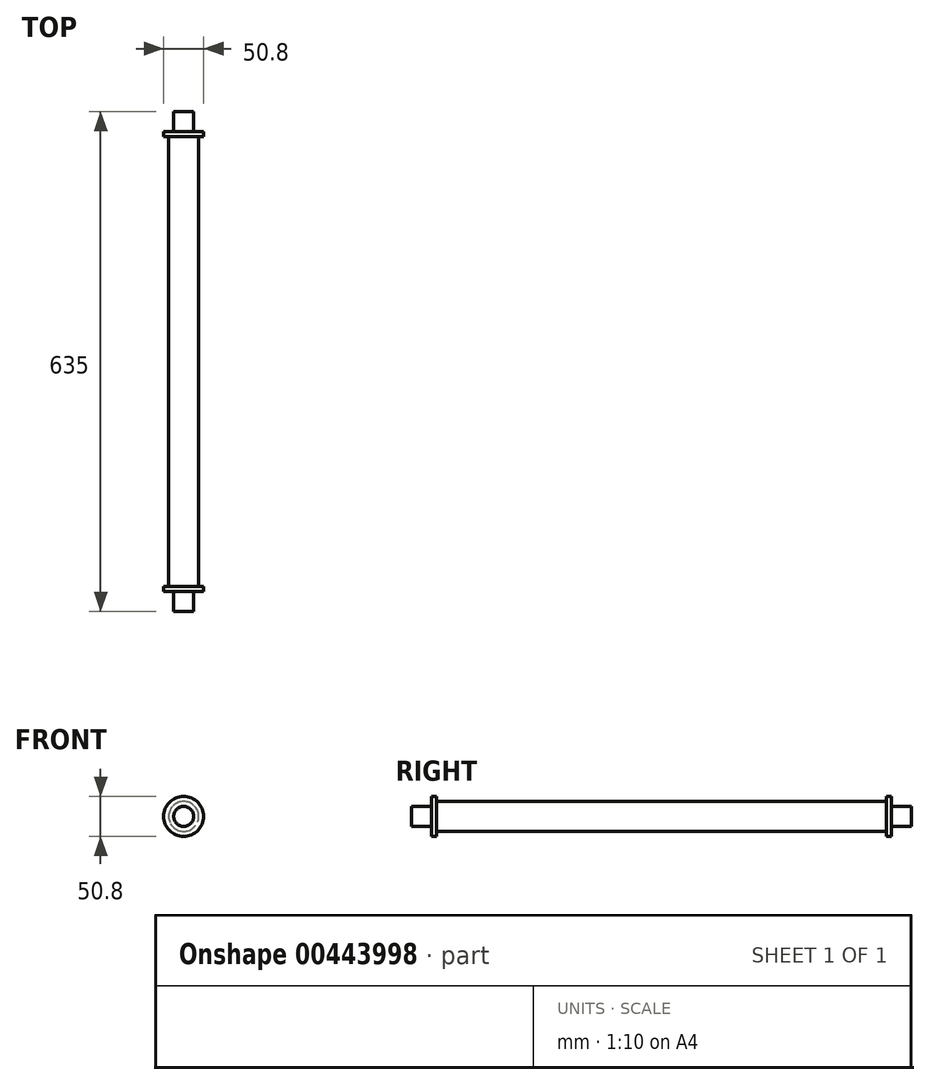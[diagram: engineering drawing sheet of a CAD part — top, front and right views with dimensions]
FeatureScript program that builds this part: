
annotation { "Feature Type Name" : "Feature", "Feature Type Description" : "" }
export const myFeature = defineFeature(function(context is Context, id is Id, definition is map)
    precondition{}
    {
        {
            var Q0;
            Q0=qCreatedBy(makeId("Front.planeOp"),FACE);
            var sketch = newSketch(context, id + "F0", { "sketchPlane" : qUnion([Q0])});
            skCircle(sketch, "E0", {"center": v(0, 0) * mm, "radius": 19.05 * mm});
            skSolve(sketch);
        }
        {
            var Q0;
            Q0 = qSketchRegion(id + "F0", true);
            extrude(context, id + "F1", {"entities" : qUnion([Q0]), "depth" : 584.2 * mm});
        }
        {
            var Q0;
            Q0=makeQuery(id+"F1.opExtrude","CAP_FACE",FACE,{"disambiguationData":[OSD([sQuery(id+"F0.wireOp",EDGE,"E0")])],"isStart":false});
            var sketch = newSketch(context, id + "F2", { "sketchPlane" : qUnion([Q0])});
            skCircle(sketch, "E1", {"center": v(0, 0) * mm, "radius": 25.4 * mm});
            skSolve(sketch);
        }
        {
            var Q0;
            Q0=makeQuery(id+"F1.opExtrude","CAP_FACE",FACE,{"disambiguationData":[OSD([sQuery(id+"F0.wireOp",EDGE,"E0")])],"isStart":true});
            var sketch = newSketch(context, id + "F3", { "sketchPlane" : qUnion([Q0])});
            skCircle(sketch, "E2", {"center": v(0, 0) * mm, "radius": 25.4 * mm});
            skSolve(sketch);
        }
        {
            var Q0;
            Q0 = qSketchRegion(id + "F3", true);
            extrude(context, id + "F4", {"entities" : qUnion([Q0]), "operationType" : NewBodyOperationType.ADD, "oppositeDirection" : true, "depth" : 6.35 * mm});
        }
        {
            var Q0;
            Q0=makeQuery(id+"F2.imprint","IMPRINT",FACE,{"disambiguationData":[TD([[makeQuery(id+"F2.imprint","IMPRINT",EDGE,{"derivedFrom":sQuery(id+"F2.wireOp",EDGE,"E1")}),1.0]])]});
            extrude(context, id + "F5", {"entities" : qUnion([Q0]), "operationType" : NewBodyOperationType.ADD, "oppositeDirection" : true, "depth" : 6.35 * mm});
        }
        {
            var Q0;
            {var subQ0=sQuery(id+"F0.wireOp",EDGE,"E0");Q0=makeQuery(id+"F5.boolean.opBoolean","MERGE",FACE,{"derivedFrom":[makeQuery(id+"F1.opExtrude","CAP_FACE",FACE,{"disambiguationData":[OSD([subQ0])],"isStart":false}),makeQuery(id+"F5.opExtrude","CAP_FACE",FACE,{"disambiguationData":[OSD([subQ0,sQuery(id+"F2.wireOp",EDGE,"E1")])],"isStart":true})]});}
            var sketch = newSketch(context, id + "F6", { "sketchPlane" : qUnion([Q0])});
            skCircle(sketch, "E3", {"center": v(0, 0) * mm, "radius": 12.7 * mm});
            skSolve(sketch);
        }
        {
            var Q0;
            Q0=makeQuery(id+"F6.imprint","IMPRINT",FACE,{"disambiguationData":[TD([[makeQuery(id+"F6.imprint","IMPRINT",EDGE,{"derivedFrom":sQuery(id+"F6.wireOp",EDGE,"E3")}),1.0]])]});
            extrude(context, id + "F7", {"entities" : qUnion([Q0]), "operationType" : NewBodyOperationType.ADD, "depth" : 25.4 * mm});
        }
        {
            var Q0;
            Q0=makeQuery(id+"F4.boolean.opBoolean","MERGE",FACE,{"derivedFrom":[makeQuery(id+"F1.opExtrude","CAP_FACE",FACE,{"disambiguationData":[OSD([sQuery(id+"F0.wireOp",EDGE,"E0")])],"isStart":true}),makeQuery(id+"F4.opExtrude","CAP_FACE",FACE,{"disambiguationData":[OSD([sQuery(id+"F3.wireOp",EDGE,"E2")])],"isStart":true})]});
            var sketch = newSketch(context, id + "F8", { "sketchPlane" : qUnion([Q0])});
            skCircle(sketch, "E4", {"center": v(0, 0) * mm, "radius": 12.7 * mm});
            skSolve(sketch);
        }
        {
            var Q0;
            Q0=makeQuery(id+"F8.imprint","IMPRINT",FACE,{"disambiguationData":[TD([[makeQuery(id+"F8.imprint","IMPRINT",EDGE,{"derivedFrom":sQuery(id+"F8.wireOp",EDGE,"E4")}),1.0]])]});
            extrude(context, id + "F9", {"entities" : qUnion([Q0]), "operationType" : NewBodyOperationType.ADD, "depth" : 25.4 * mm});
        }
    });
